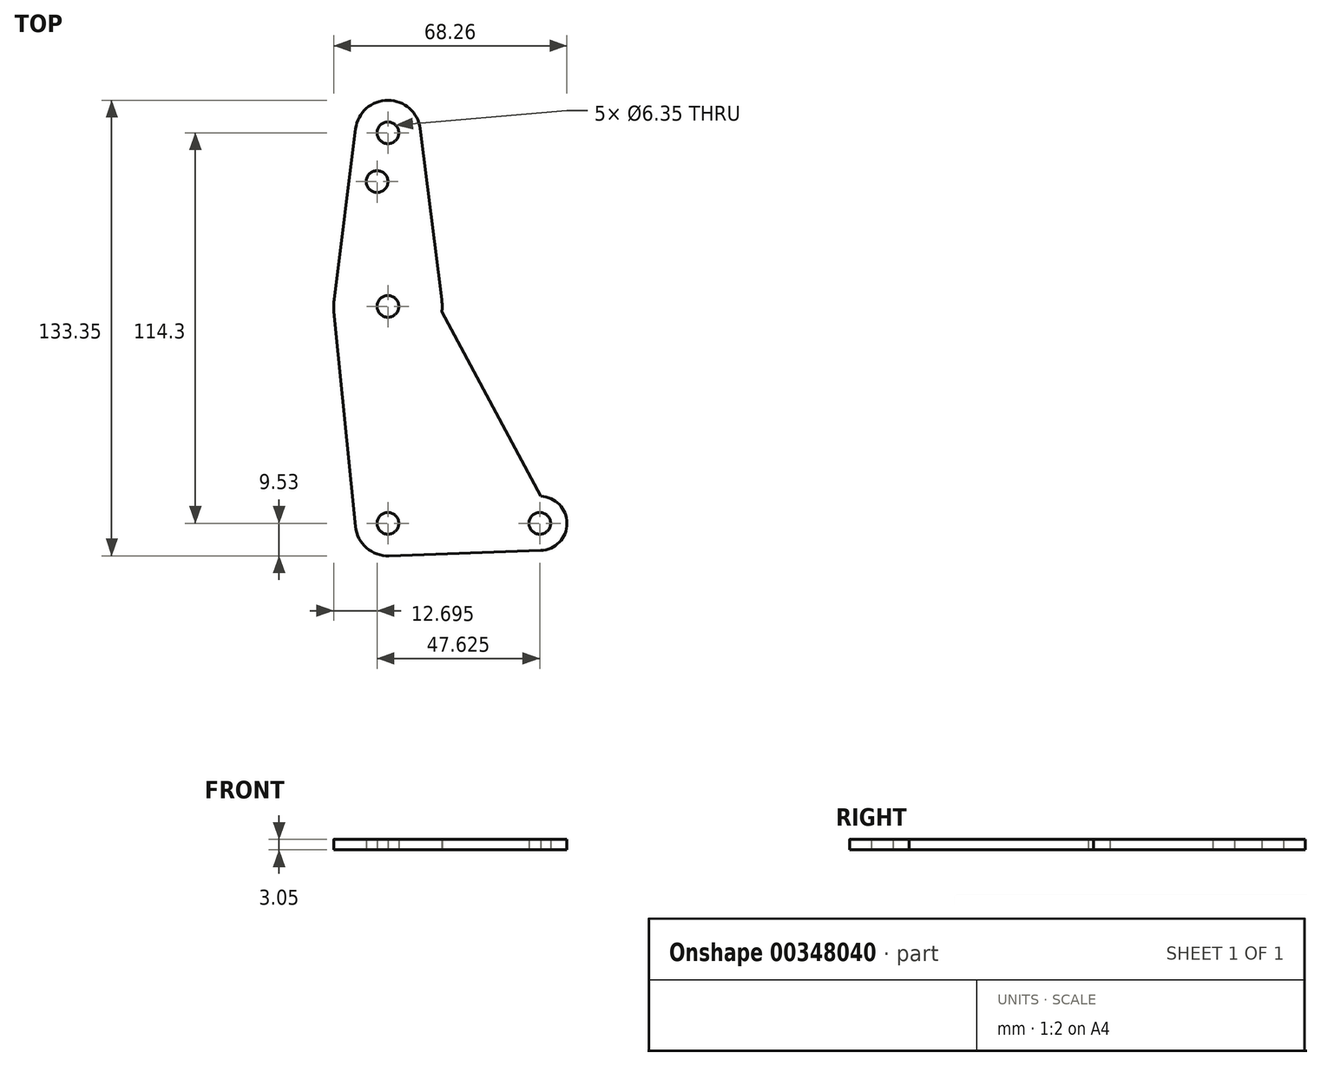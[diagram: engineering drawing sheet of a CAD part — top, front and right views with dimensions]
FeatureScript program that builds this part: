
annotation { "Feature Type Name" : "Feature", "Feature Type Description" : "" }
export const myFeature = defineFeature(function(context is Context, id is Id, definition is map)
    precondition{}
    {
        {
            var Q0;
            Q0=qCreatedBy(makeId("Top.planeOp"),FACE);
            var sketch = newSketch(context, id + "F0", { "sketchPlane" : qUnion([Q0])});
            skCircle(sketch, "E0", {"center": v(0, 0) * mm, "radius": 15.88 * mm});
            skCircle(sketch, "E1", {"center": v(0, 50.8) * mm, "radius": 9.53 * mm});
            skCircle(sketch, "E2", {"center": v(0, -63.5) * mm, "radius": 9.53 * mm});
            skCircle(sketch, "E3", {"center": v(44.45, -63.5) * mm, "radius": 7.94 * mm});
            skCircle(sketch, "E4", {"center": v(-3.18, 36.53) * mm, "radius": 3.18 * mm});
            skLineSegment(sketch, "E5", {"start": v(-9.45, 52) * mm, "end": v(-15.75, 1.98) * mm});
            skLineSegment(sketch, "E6", {"start": v(9.45, 52) * mm, "end": v(15.75, 1.98) * mm});
            skLineSegment(sketch, "E7", {"start": v(-9.48, -64.45) * mm, "end": v(-15.8, -1.59) * mm});
            skCircle(sketch, "E8", {"center": v(0, 50.8) * mm, "radius": 3.18 * mm});
            skCircle(sketch, "E9", {"center": v(0, 0) * mm, "radius": 3.18 * mm});
            skCircle(sketch, "E10", {"center": v(0, -63.5) * mm, "radius": 3.18 * mm});
            skCircle(sketch, "E11", {"center": v(44.45, -63.5) * mm, "radius": 3.18 * mm});
            skLineSegment(sketch, "E12", {"start": v(-3.18, 36.53) * mm, "end": v(0, 36.53) * mm, "construction": true});
            skLineSegment(sketch, "E13", {"start": v(0, 36.53) * mm, "end": v(0, 0) * mm, "construction": true});
            skLineSegment(sketch, "E14", {"start": v(0, -63.5) * mm, "end": v(0, 0) * mm, "construction": true});
            skLineSegment(sketch, "E15", {"start": v(0, -63.5) * mm, "end": v(44.45, -63.5) * mm, "construction": true});
            skLineSegment(sketch, "E16", {"start": v(0.34, -73.02) * mm, "end": v(44.73, -71.43) * mm});
            skLineSegment(sketch, "E17", {"start": v(0, 50.8) * mm, "end": v(0, -63.5) * mm, "construction": true});
            skLineSegment(sketch, "E18", {"start": v(15.8, -1.59) * mm, "end": v(11.34, -45.9) * mm});
            skLineSegment(sketch, "E19", {"start": v(18.97, -54.65) * mm, "end": v(44.73, -55.57) * mm});
            skArc(sketch, "E20.filletArc", {"start": v(11.34, -45.9) * mm, "mid": v(13.26, -51.93) * mm, "end": v(18.97, -54.65) * mm});
            skLineSegment(sketch, "E21", {"start": v(15.8, -1.59) * mm, "end": v(44.73, -55.57) * mm});
            skSolve(sketch);
        }
        {
            var Q0;
            Q0 = qSketchRegion(id + "F0", true);
            extrude(context, id + "F1", {"entities" : qUnion([Q0]), "depth" : 3.05 * mm});
        }
    });
